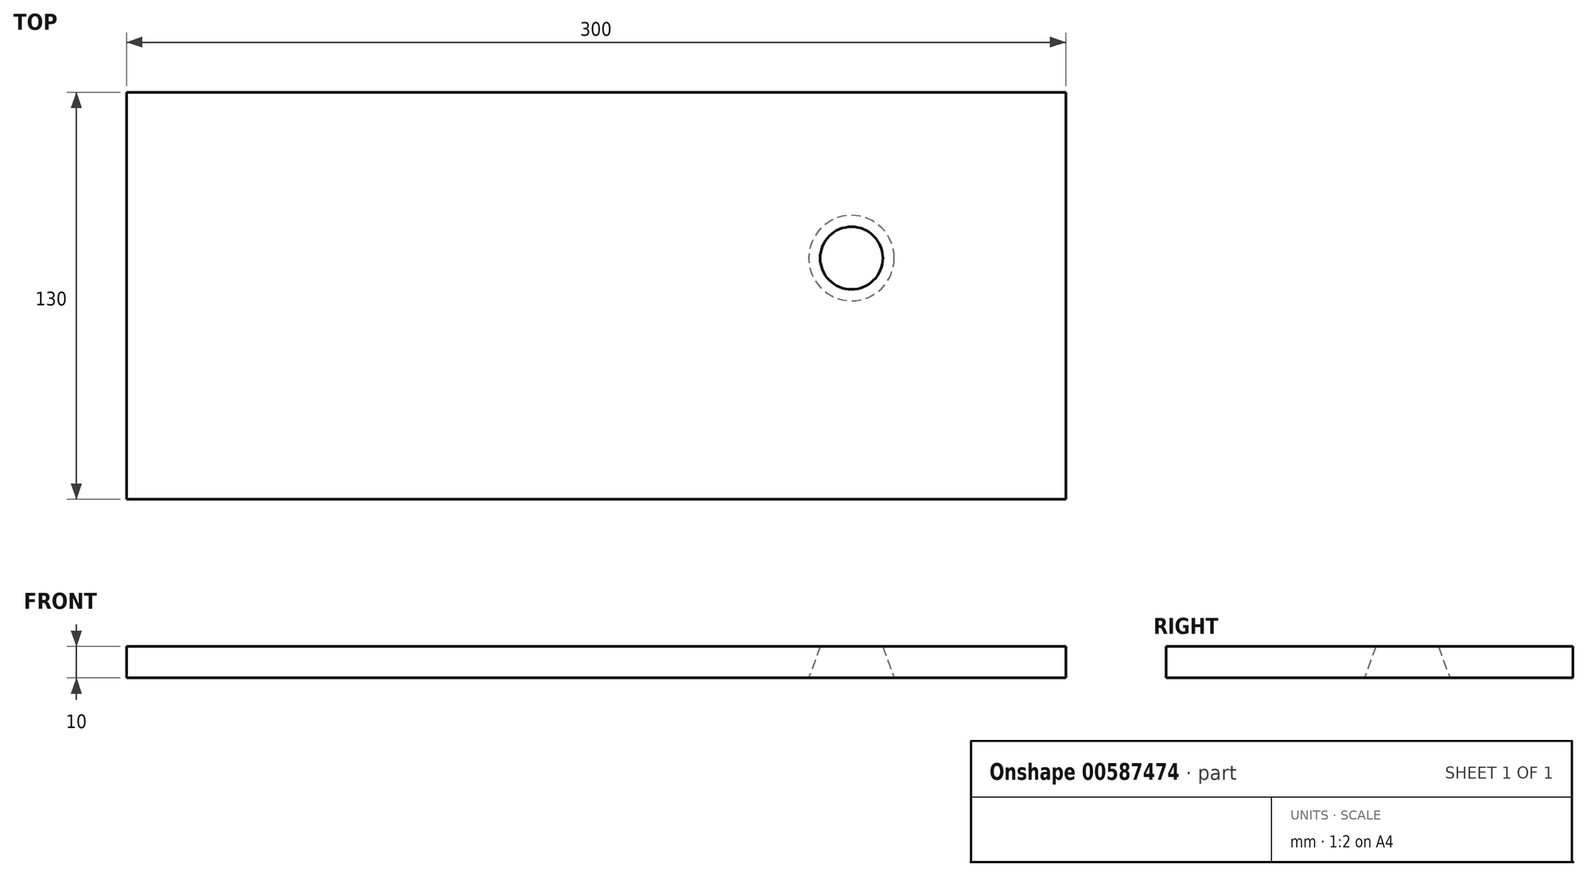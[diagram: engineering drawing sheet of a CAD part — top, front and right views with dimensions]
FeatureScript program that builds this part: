
annotation { "Feature Type Name" : "Feature", "Feature Type Description" : "" }
export const myFeature = defineFeature(function(context is Context, id is Id, definition is map)
    precondition{}
    {
        {
            var Q0;
            Q0=qCreatedBy(makeId("Top.planeOp"),FACE);
            var sketch = newSketch(context, id + "F0", { "sketchPlane" : qUnion([Q0])});
            skLineSegment(sketch, "E0.bottom", {"start": v(-109.05, -54.64) * mm, "end": v(190.95, -54.64) * mm});
            skLineSegment(sketch, "E0.top", {"start": v(-109.05, 75.36) * mm, "end": v(190.95, 75.36) * mm});
            skLineSegment(sketch, "E0.left", {"start": v(-109.05, -54.64) * mm, "end": v(-109.05, 75.36) * mm});
            skLineSegment(sketch, "E0.right", {"start": v(190.95, -54.64) * mm, "end": v(190.95, 75.36) * mm});
            skSolve(sketch);
        }
        {
            var Q0;
            Q0=makeQuery(id+"F0.imprint","IMPRINT",FACE,{"disambiguationData":[TD([[makeQuery(id+"F0.imprint","IMPRINT",EDGE,{"derivedFrom":sQuery(id+"F0.wireOp",EDGE,"E0.bottom")}),1.0]])]});
            extrude(context, id + "F1", {"entities" : qUnion([Q0]), "depth" : 10 * mm, "offsetDistance" : 25 * mm});
        }
        {
            var Q0;
            Q0=makeQuery(id+"F1.opExtrude","CAP_FACE",FACE,{"disambiguationData":[OSD([sQuery(id+"F0.wireOp",EDGE,"E0.bottom"),sQuery(id+"F0.wireOp",EDGE,"E0.top"),sQuery(id+"F0.wireOp",EDGE,"E0.left"),sQuery(id+"F0.wireOp",EDGE,"E0.right")])],"isStart":false});
            var sketch = newSketch(context, id + "F2", { "sketchPlane" : qUnion([Q0])});
            skCircle(sketch, "E1", {"center": v(122.5, 22.4) * mm, "radius": 10 * mm});
            skSolve(sketch);
        }
        {
            var Q0;
            Q0 = qSketchRegion(id + "F2", true);
            extrude(context, id + "F3", {"entities" : qUnion([Q0]), "operationType" : NewBodyOperationType.REMOVE, "oppositeDirection" : true, "depth" : 25 * mm, "offsetDistance" : 25 * mm, "hasDraft" : true, "draftAngle" : 20 * degree});
        }
    });
